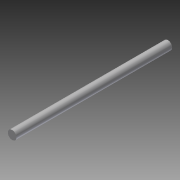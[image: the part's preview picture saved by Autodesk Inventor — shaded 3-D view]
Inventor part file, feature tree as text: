
AUTODESK INVENTOR PART (.ipt)
format: ipt  version: 2014 (Build 180170000, 170)  size: 72,192 bytes
history: native  units: in
note: dims shown in document units (in); Inventor stores cm internally (conversion verified against a paired STEP export)
features: extrude x1, sketch x1
ambient origin geometry x8: Origin, YZ Plane, XZ Plane, XY Plane, X Axis, Y Axis, Z Axis, Center Point
bodies: Solid1 (feature_tree)
feature tree (2):
  extrude  "Extrusion1"  Depth=7.0in TaperAngle=0.0deg
  sketch  "Sketch1"  dims[d0=0.5in d1=7.0in d2=0.0in d3=0.028in]
